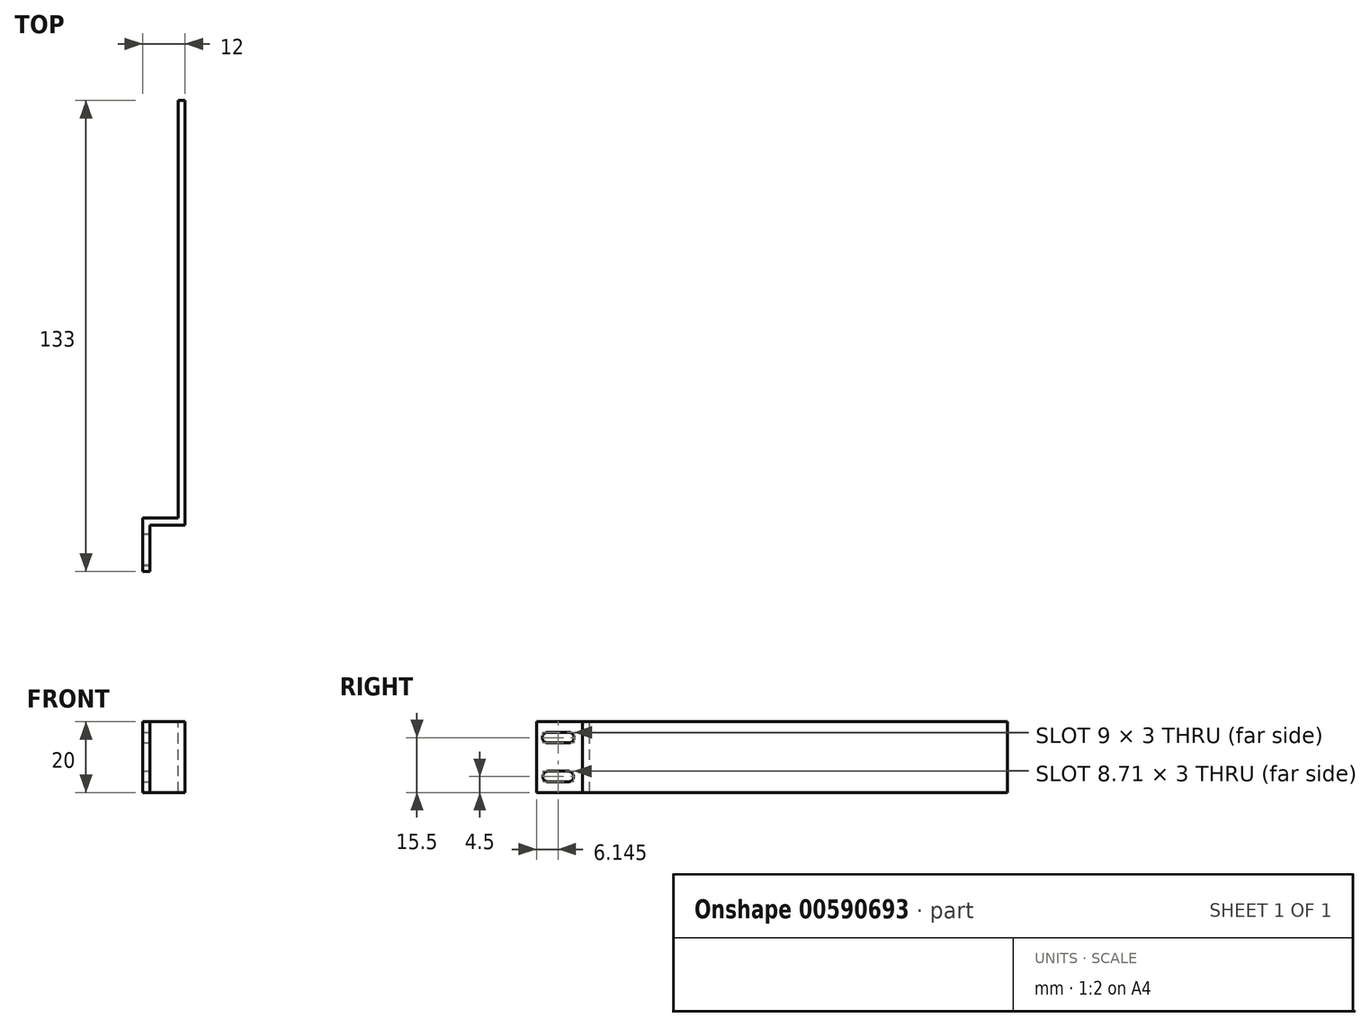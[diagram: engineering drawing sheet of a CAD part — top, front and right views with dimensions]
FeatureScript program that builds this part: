
annotation { "Feature Type Name" : "Feature", "Feature Type Description" : "" }
export const myFeature = defineFeature(function(context is Context, id is Id, definition is map)
    precondition{}
    {
        {
            var Q0;
            Q0=qCreatedBy(makeId("Right.planeOp"),FACE);
            var sketch = newSketch(context, id + "F0", { "sketchPlane" : qUnion([Q0])});
            skLineSegment(sketch, "E0.bottom", {"start": v(60, -10) * mm, "end": v(-60, -10) * mm});
            skLineSegment(sketch, "E0.top", {"start": v(60, 10) * mm, "end": v(-60, 10) * mm});
            skLineSegment(sketch, "E0.left", {"start": v(60, -10) * mm, "end": v(60, 10) * mm});
            skLineSegment(sketch, "E0.right", {"start": v(-60, -10) * mm, "end": v(-60, 10) * mm});
            skPoint(sketch, "E0.middle", {"position": v(0, 0) * mm});
            skSolve(sketch);
        }
        {
            var Q0;
            Q0 = qSketchRegion(id + "F0", true);
            extrude(context, id + "F1", {"entities" : qUnion([Q0]), "depth" : 2 * mm, "offsetDistance" : 25 * mm});
        }
        {
            var Q0;
            Q0=makeQuery(id+"F1.opExtrude","SWEPT_FACE",FACE,{"disambiguationData":[OSD([sQuery(id+"F0.wireOp",EDGE,"E0.right")])]});
            var sketch = newSketch(context, id + "F2", { "sketchPlane" : qUnion([Q0])});
            skLineSegment(sketch, "E1.0", {"start": v(2, -10) * mm, "end": v(2, 10) * mm});
            skLineSegment(sketch, "E2", {"start": v(2, 10) * mm, "end": v(-8, 10) * mm});
            skLineSegment(sketch, "E3", {"start": v(-8, 10) * mm, "end": v(-8, -10) * mm});
            skLineSegment(sketch, "E4", {"start": v(-8, -10) * mm, "end": v(2, -10) * mm});
            skSolve(sketch);
        }
        {
            var Q0;
            {var subQ2=sQuery(id+"F2.wireOp",EDGE,"E3");Q0=makeQuery(id+"F2.imprint","IMPRINT",FACE,{"disambiguationData":[TD([[makeQuery(id+"F2.imprint","IMPRINT",EDGE,{"derivedFrom":subQ2}),1.0]])]});}
            extrude(context, id + "F3", {"entities" : qUnion([Q0]), "operationType" : NewBodyOperationType.ADD, "oppositeDirection" : true, "depth" : 2 * mm, "offsetDistance" : 25 * mm});
        }
        {
            var Q0;
            Q0=makeQuery(id+"F3.opExtrude","SWEPT_FACE",FACE,{"disambiguationData":[OSD([sQuery(id+"F2.wireOp",EDGE,"E3")])]});
            var sketch = newSketch(context, id + "F4", { "sketchPlane" : qUnion([Q0])});
            skLineSegment(sketch, "E5.0", {"start": v(58, 10) * mm, "end": v(58, -10) * mm});
            skLineSegment(sketch, "E6", {"start": v(58, -10) * mm, "end": v(73, -10) * mm});
            skLineSegment(sketch, "E7", {"start": v(73, -10) * mm, "end": v(73, 10) * mm});
            skLineSegment(sketch, "E8", {"start": v(73, 10) * mm, "end": v(58, 10) * mm});
            skLineSegment(sketch, "E9", {"start": v(66.86, -5) * mm, "end": v(66.86, 5) * mm, "construction": true});
            skLineSegment(sketch, "E10.bottom", {"start": v(63.86, 4.5) * mm, "end": v(69.86, 4.5) * mm});
            skLineSegment(sketch, "E10.top", {"start": v(63.86, 5.5) * mm, "end": v(69.86, 5.5) * mm});
            skLineSegment(sketch, "E10.left", {"start": v(63.86, 4.5) * mm, "end": v(63.86, 5.5) * mm});
            skLineSegment(sketch, "E10.right", {"start": v(69.86, 4.5) * mm, "end": v(69.86, 5.5) * mm});
            skPoint(sketch, "E10.middle", {"position": v(66.86, 5) * mm});
            skArc(sketch, "E11.0.startCap", {"start": v(63.86, 4) * mm, "mid": v(62.36, 5.5) * mm, "end": v(63.86, 7) * mm});
            skArc(sketch, "E11.0.endCap", {"start": v(69.86, 7) * mm, "mid": v(71.36, 5.5) * mm, "end": v(69.86, 4) * mm});
            skLineSegment(sketch, "E11.0.left", {"start": v(63.86, 7) * mm, "end": v(69.86, 7) * mm});
            skLineSegment(sketch, "E11.0.right", {"start": v(63.86, 4) * mm, "end": v(69.86, 4) * mm});
            skLineSegment(sketch, "E12.bottom", {"start": v(64, -5.5) * mm, "end": v(69.71, -5.5) * mm});
            skLineSegment(sketch, "E12.top", {"start": v(64, -4.5) * mm, "end": v(69.71, -4.5) * mm});
            skLineSegment(sketch, "E12.left", {"start": v(64, -5.5) * mm, "end": v(64, -4.5) * mm});
            skLineSegment(sketch, "E12.right", {"start": v(69.71, -5.5) * mm, "end": v(69.71, -4.5) * mm});
            skPoint(sketch, "E12.middle", {"position": v(66.86, -5) * mm});
            skArc(sketch, "E13.0.startCap", {"start": v(64, -7) * mm, "mid": v(62.5, -5.5) * mm, "end": v(64, -4) * mm});
            skArc(sketch, "E13.0.endCap", {"start": v(69.71, -4) * mm, "mid": v(71.21, -5.5) * mm, "end": v(69.71, -7) * mm});
            skLineSegment(sketch, "E13.0.left", {"start": v(64, -4) * mm, "end": v(69.71, -4) * mm});
            skLineSegment(sketch, "E13.0.right", {"start": v(64, -7) * mm, "end": v(69.71, -7) * mm});
            skSolve(sketch);
        }
        {
            var Q0;
            Q0 = qSketchRegion(id + "F4", true);
            extrude(context, id + "F5", {"entities" : qUnion([Q0]), "operationType" : NewBodyOperationType.ADD, "depth" : 2 * mm, "offsetDistance" : 25 * mm});
        }
    });
